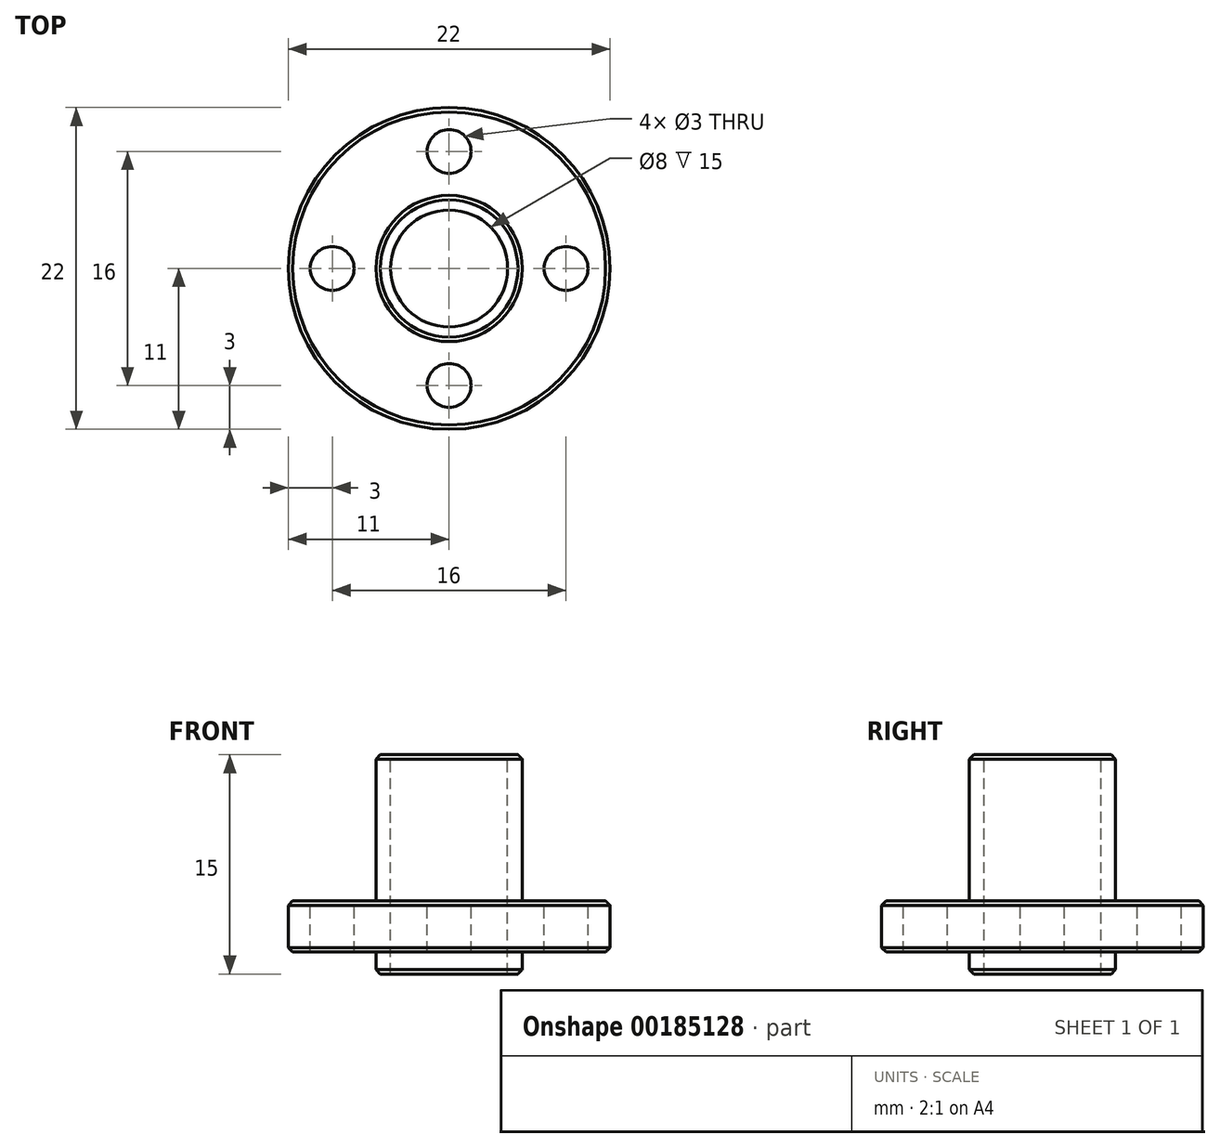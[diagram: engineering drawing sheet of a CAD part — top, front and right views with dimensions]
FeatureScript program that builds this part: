
annotation { "Feature Type Name" : "Feature", "Feature Type Description" : "" }
export const myFeature = defineFeature(function(context is Context, id is Id, definition is map)
    precondition{}
    {
        {
            var Q0;
            Q0=qCreatedBy(makeId("Front.planeOp"),FACE);
            var sketch = newSketch(context, id + "F0", { "sketchPlane" : qUnion([Q0])});
            skLineSegment(sketch, "E0", {"start": v(0, 21.78) * mm, "end": v(0, -28) * mm, "construction": true});
            skLineSegment(sketch, "E1.bottom", {"start": v(-4, 0) * mm, "end": v(-5, 0) * mm});
            skLineSegment(sketch, "E1.top", {"start": v(-4, 15) * mm, "end": v(-5, 15) * mm});
            skLineSegment(sketch, "E1.left", {"start": v(-4, 0) * mm, "end": v(-4, 15) * mm});
            skLineSegment(sketch, "E1.right", {"start": v(-5, 0) * mm, "end": v(-5, 1.5) * mm});
            skLineSegment(sketch, "E2.bottom", {"start": v(-5, 1.5) * mm, "end": v(-11, 1.5) * mm});
            skLineSegment(sketch, "E2.top", {"start": v(-5, 5) * mm, "end": v(-11, 5) * mm});
            skLineSegment(sketch, "E2.right", {"start": v(-11, 1.5) * mm, "end": v(-11, 5) * mm});
            skLineSegment(sketch, "E3.trimOffspring", {"start": v(-5, 5) * mm, "end": v(-5, 15) * mm});
            skSolve(sketch);
        }
        {
            var Q0;
            Q0 = qSketchRegion(id + "F0", true);
            var Q1;
            Q1=sQuery(id+"F0.wireOp",EDGE,"E0");
            revolve(context, id + "F1", {"entities" : qUnion([Q0]), "axis" : qUnion([Q1]), "revolveType" : RevolveType.FULL});
        }
        {
            var Q0;
            Q0=makeQuery(id+"F1.opRevolve","SWEPT_EDGE",EDGE,{"disambiguationData":[OSD([sQuery(id+"F0.wireOp",EDGE,"E2.top"),sQuery(id+"F0.wireOp",EDGE,"E2.right")])]});
            var Q1;
            Q1=makeQuery(id+"F1.opRevolve","SWEPT_EDGE",EDGE,{"disambiguationData":[OSD([sQuery(id+"F0.wireOp",EDGE,"E1.top"),sQuery(id+"F0.wireOp",EDGE,"E3.trimOffspring")])]});
            var Q2;
            Q2=makeQuery(id+"F1.opRevolve","SWEPT_EDGE",EDGE,{"disambiguationData":[OSD([sQuery(id+"F0.wireOp",EDGE,"E2.bottom"),sQuery(id+"F0.wireOp",EDGE,"E2.right")])]});
            var Q3;
            Q3=makeQuery(id+"F1.opRevolve","SWEPT_EDGE",EDGE,{"disambiguationData":[OSD([sQuery(id+"F0.wireOp",EDGE,"E1.bottom"),sQuery(id+"F0.wireOp",EDGE,"E1.right")])]});
            chamfer(context, id + "F2", {"entities" : qUnion([Q0, Q1, Q2, Q3]), "width" : 0.3 * mm, "tangentPropagation" : true});
        }
        {
            var Q0;
            Q0=makeQuery(id+"F1.opRevolve","SWEPT_FACE",FACE,{"disambiguationData":[OSD([sQuery(id+"F0.wireOp",EDGE,"E2.top")])]});
            var sketch = newSketch(context, id + "F3", { "sketchPlane" : qUnion([Q0])});
            skCircle(sketch, "E4", {"center": v(0, 8) * mm, "radius": 1.5 * mm});
            skCircle(sketch, "E5.1.0", {"center": v(-8, 0) * mm, "radius": 1.5 * mm});
            skCircle(sketch, "E5.2.0", {"center": v(0, -8) * mm, "radius": 1.5 * mm});
            skCircle(sketch, "E5.3.0", {"center": v(8, 0) * mm, "radius": 1.5 * mm});
            skPoint(sketch, "E5.center", {"position": v(0, 0) * mm});
            skSolve(sketch);
        }
        {
            var Q0;
            Q0 = qSketchRegion(id + "F3", true);
            extrude(context, id + "F4", {"entities" : qUnion([Q0]), "operationType" : NewBodyOperationType.REMOVE, "oppositeDirection" : true, "depth" : 25 * mm});
        }
    });
